# Revit family: Plumbing-Fix_Faucet-Touchless_Stern_Tubular-XL
name_source: partatom
category: Plumbing Fixtures
units: mm (PartAtom-declared; Revit-internal decimal feet)

## family parameters
Classification Number = 23.45.55.14
Cut with Voids When Loaded = No
Enable Cutting in Views = No
Host = Face
Maintain Annotation Orientation = No
Part Type = Normal
Room Calculation Point = No
Round Connector Dimension = Use Diameter
Shared = No

## types (10) — shared parameters
Assembly Code = D2010300
Available Options = as Specified
CW Connection = Yes
CWFU = 1
Default Elevation = 0' - 0"
HW Connection = Yes
HWFU = 1
Keynote = 22 40 00
Manufacturer = Stern Engineering
Manufacturer Website = http://www.sternfaucets.com
Operating Pressure Range = 7.26 - 116 PSI  ;  0.5 - 8 bar
Operating Temperature Range = Up to 149 F / 65 C
Piping_Flow = 0 GPM
Piping_Inlet Diameter = 1"
Product Data = http://www.arcat.com
Product Features = as Specified
Revision = R1_2018-04
Sales Information = http://www.sternfaucets.com
Spout Height = 0' - 2 1/4"
Spout Reach = 0' - 0"
Standards Conformance = as Specified
Type Comments = as Specified
URL = http://www.sternfaucets.com
Unit Height = 0' - 0"
Unit Width = 0' - 2"
Vent Connection = No
Warranty Duration (Years) = 2
Waste Connection = No
zero-valued in all types: Cost, Expected Lifespan (Years), Maintenance Schedule (Months), WFU

## per-type parameters (varying)
| type | Description | Model | Power Supply |
| Battery Pack 1.58 GPM | Stern Touchless Wall Mounted Faucet - Tubular XLB as Specified | Tubular XLB | 9V Battery |
| Battery Pack 1 GPM | Stern Touchless Wall Mounted Faucet - Tubular XLB as Specified | Tubular XLB | 9V Battery |
| Battery Pack 0.8 GPM | Stern Touchless Wall Mounted Faucet - Tubular XLB as Specified | Tubular XLB | 9V Battery |
| Battery Pack 0.5 GPM | Stern Touchless Wall Mounted Faucet - Tubular XLB as Specified | Tubular XLB | 9V Battery |
| Battery Pack 0.35 GPM | Stern Touchless Wall Mounted Faucet - Tubular XLB as Specified | Tubular XLB | 9V Battery |
| Transformer 1.58 GPM | Stern Touchless Wall Mounted Faucet - Tubular XLE as Specified | Tubular XLE | 9V Transformer |
| Transformer 1 GPM | Stern Touchless Wall Mounted Faucet - Tubular XLE as Specified | Tubular XLE | 9V Transformer |
| Transformer 0.8 GPM | Stern Touchless Wall Mounted Faucet - Tubular XLE as Specified | Tubular XLE | 9V Transformer |
| Transformer 0.5 GPM | Stern Touchless Wall Mounted Faucet - Tubular XLE as Specified | Tubular XLE | 9V Transformer |
| Transformer 0.35 GPM | Stern Touchless Wall Mounted Faucet - Tubular XLE as Specified | Tubular XLE | 9V Transformer |

## geometry (parser evidence)
native form markers: Sweep x2
no freeform markers — native parametric forms only
